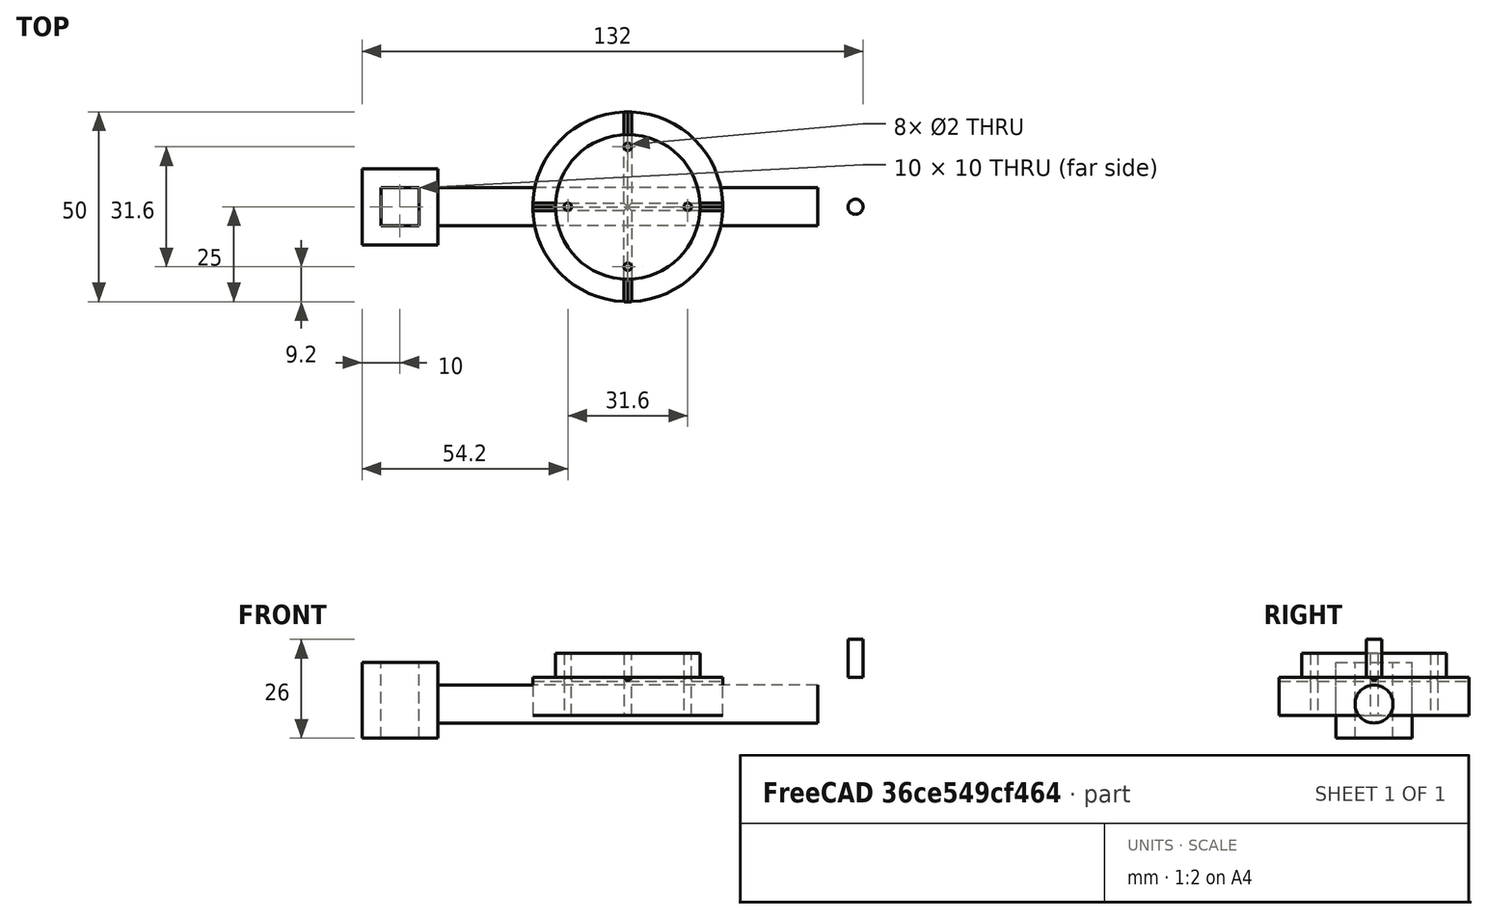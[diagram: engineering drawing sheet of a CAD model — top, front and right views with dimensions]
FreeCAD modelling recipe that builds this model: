
FCSTD DOCUMENT  (FreeCAD 0.21R33771 (Git))
Label: Stereotax_ArmAttachment
License: All rights reserved
LicenseURL: http://en.wikipedia.org/wiki/All_rights_reserved
objects: Part::FeaturePython×8, Part::Cylinder×6, Part::Cut×4, Part::MultiFuse×3, Part::Box×3
note: 24 computed .brp shape members not serialized (recipe doc carries the construction recipe); baked Part::Feature solids carry a one-line shape summary decoded from their .brp

FEATURE [Part::Cylinder] Cylinder
  Angle = 360
  AttacherType = Attacher::AttachEngine3D
  FirstAngle = 0
  Height = 6.35
  Radius = 19.05
  SecondAngle = 0
FEATURE [Part::Cylinder] Cylinder001
  Angle = 360
  AttacherType = Attacher::AttachEngine3D
  FirstAngle = 0
  Height = 10
  Placement = pos=(15.8,0,0) rot=(0,0,1;0rad)
  Radius = 1
  SecondAngle = 0
FEATURE [Part::FeaturePython] Clone  label="Cylinder002"  # Draft clone (typed FeaturePython)
  AttacherType = Attacher::AttachEngine3D
  Fuse = false
  Objects = -> [Cylinder001]
  Placement = pos=(-15.8,0,0) rot=(0,0,1;0rad)
  Scale = (1,1,1)
FEATURE [Part::FeaturePython] Clone001  label="Cylinder003"  # Draft clone (typed FeaturePython)
  AttacherType = Attacher::AttachEngine3D
  Fuse = false
  Objects = -> [Clone]
  Placement = pos=(0,15.8,0) rot=(0,0,1;0rad)
  Scale = (1,1,1)
FEATURE [Part::FeaturePython] Clone002  label="Cylinder004"  # Draft clone (typed FeaturePython)
  AttacherType = Attacher::AttachEngine3D
  Fuse = false
  Objects = -> [Clone001]
  Placement = pos=(0,-15.8,0) rot=(0,0,1;0rad)
  Scale = (1,1,1)
FEATURE [Part::MultiFuse] Fusion
  Shapes = -> [Clone002,Cylinder001,Clone,Clone001]
FEATURE [Part::Cut] Cut
  Base = -> Cylinder
  Tool = -> Fusion
FEATURE [Part::Cylinder] Cylinder002  label="Cylinder008"
  Angle = 360
  AttacherType = Attacher::AttachEngine3D
  FirstAngle = 0
  Height = 10
  Radius = 25
  SecondAngle = 0
FEATURE [Part::Cylinder] Cylinder003  label="Cylinder009"
  Angle = 360
  AttacherType = Attacher::AttachEngine3D
  FirstAngle = 0
  Height = 10
  Placement = pos=(15.8,0,0) rot=(0,0,1;0rad)
  Radius = 1
  SecondAngle = 0
FEATURE [Part::FeaturePython] Clone003  label="Cylinder005"  # Draft clone (typed FeaturePython)
  AttacherType = Attacher::AttachEngine3D
  Fuse = false
  Objects = -> [Cylinder003]
  Placement = pos=(-15.8,0,0) rot=(0,0,1;0rad)
  Scale = (1,1,1)
FEATURE [Part::FeaturePython] Clone004  label="Cylinder006"  # Draft clone (typed FeaturePython)
  AttacherType = Attacher::AttachEngine3D
  Fuse = false
  Objects = -> [Clone003]
  Placement = pos=(0,15.8,0) rot=(0,0,1;0rad)
  Scale = (1,1,1)
FEATURE [Part::FeaturePython] Clone005  label="Cylinder007"  # Draft clone (typed FeaturePython)
  AttacherType = Attacher::AttachEngine3D
  Fuse = false
  Objects = -> [Clone004]
  Placement = pos=(0,-15.8,0) rot=(0,0,1;0rad)
  Scale = (1,1,1)
FEATURE [Part::MultiFuse] Fusion001
  Shapes = -> [Clone005,Cylinder003,Clone003,Clone004]
FEATURE [Part::Cut] Cut001
  Base = -> Cylinder002
  Placement = pos=(0,0,-10) rot=(0,0,1;0rad)
  Tool = -> Fusion001
FEATURE [Part::Box] Box  label="Cube"
  AttacherType = Attacher::AttachEngine3D
  Height = 10
  Length = 60
  Placement = pos=(-30,0,-0.5) rot=(1,0,0;0.785398rad)
  Width = 10
FEATURE [Part::FeaturePython] Clone006  label="Cube001"  # Draft clone (typed FeaturePython)
  AttacherType = Attacher::AttachEngine3D
  Fuse = false
  Objects = -> [Box]
  Placement = pos=(-6.7e-15,-30,-0.5) rot=(0.357407,0.357407,0.862856;1.71777rad)
  Scale = (1,1,1)
FEATURE [Part::MultiFuse] Fusion002
  Placement = pos=(0,0,-0.5) rot=(0,0,1;0rad)
  Shapes = -> [Clone006,Box]
FEATURE [Part::Cut] Cut002
  Base = -> Cut001
  Tool = -> Fusion002
FEATURE [Part::Cylinder] Cylinder004  label="Cylinder010"
  Angle = 360
  AttacherType = Attacher::AttachEngine3D
  FirstAngle = 0
  Height = 100
  Placement = pos=(-50,0,-7) rot=(0,1,0;1.5708rad)
  Radius = 5
  SecondAngle = 0
FEATURE [Part::Box] Box001  label="Cube002"
  AttacherType = Attacher::AttachEngine3D
  Height = 20
  Length = 20
  Placement = pos=(50,-10,-16) rot=(0,0,1;0rad)
  Width = 20
FEATURE [Part::Box] Box002  label="Cube003"
  AttacherType = Attacher::AttachEngine3D
  Height = 20
  Length = 10
  Placement = pos=(55,-5,-16) rot=(0,0,1;0rad)
  Width = 10
FEATURE [Part::Cut] Cut003  label="Clamp_1"
  Base = -> Box001
  Tool = -> Box002
FEATURE [Part::FeaturePython] Clone007  label="Clamp_002"  # Draft clone (typed FeaturePython)
  AttacherType = Attacher::AttachEngine3D
  Fuse = false
  Objects = -> [Cut003]
  Placement = pos=(-120,0,0) rot=(0,0,1;0rad)
  Scale = (1,1,1)
FEATURE [Part::Cylinder] Cylinder005  label="Cylinder011"
  Angle = 360
  AttacherType = Attacher::AttachEngine3D
  FirstAngle = 0
  Height = 10
  Placement = pos=(60,0,0) rot=(0,0,1;1.5708rad)
  Radius = 2
  SecondAngle = 0
